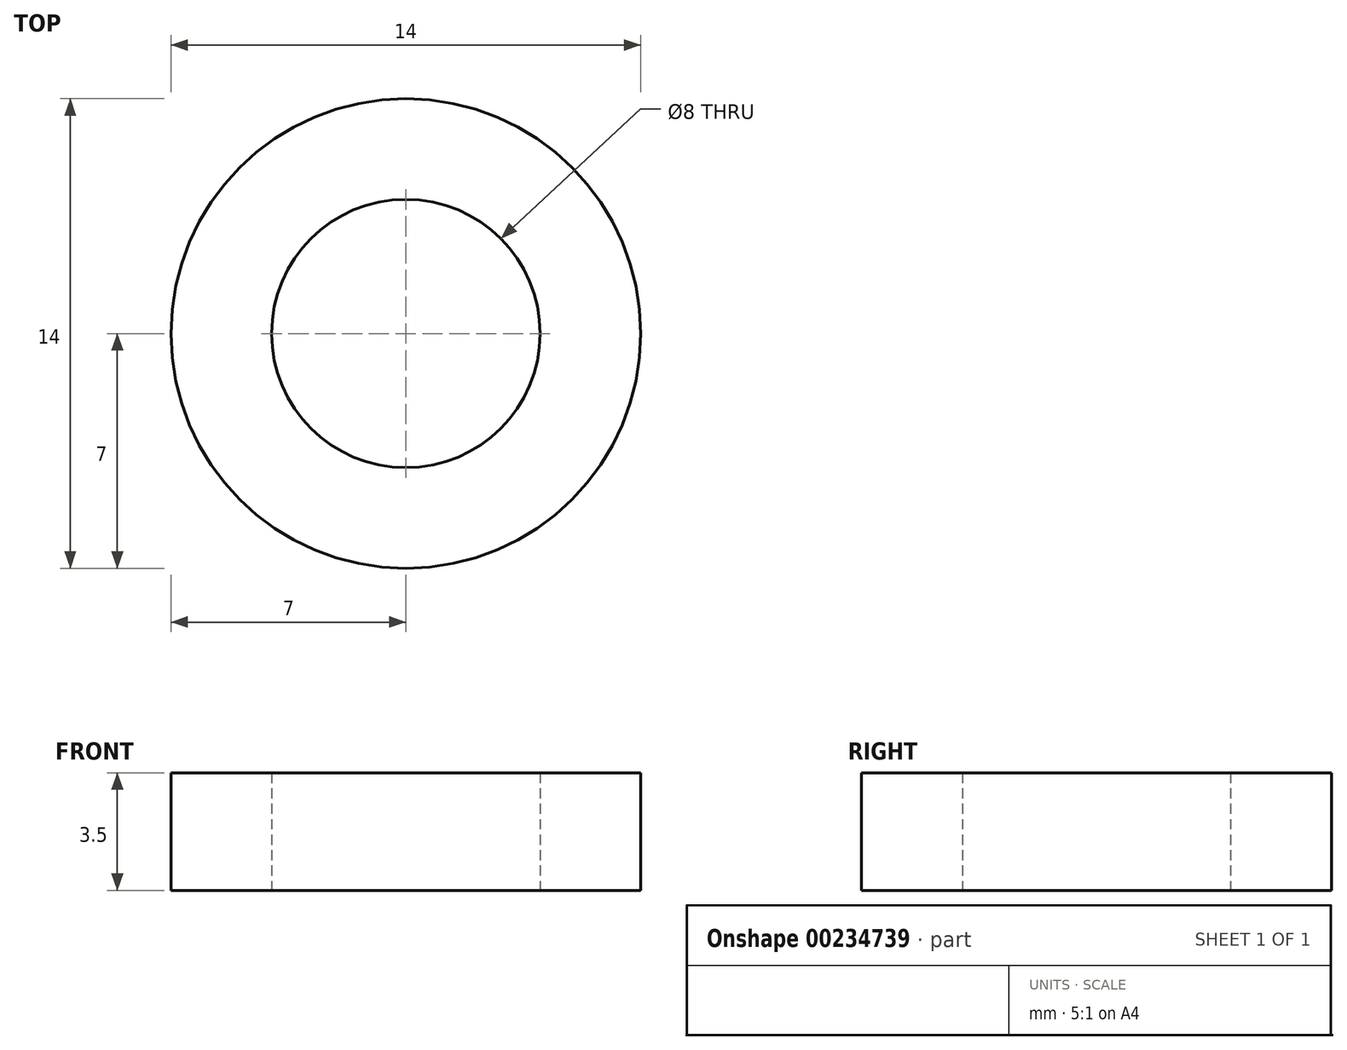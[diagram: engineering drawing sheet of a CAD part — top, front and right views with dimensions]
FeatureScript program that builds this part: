
annotation { "Feature Type Name" : "Feature", "Feature Type Description" : "" }
export const myFeature = defineFeature(function(context is Context, id is Id, definition is map)
    precondition{}
    {
        {
            var Q0;
            Q0=qCreatedBy(makeId("Top.planeOp"),FACE);
            var sketch = newSketch(context, id + "F0", { "sketchPlane" : qUnion([Q0])});
            skCircle(sketch, "E0", {"center": v(0, 0) * mm, "radius": 7 * mm});
            skCircle(sketch, "E1", {"center": v(0, 0) * mm, "radius": 4 * mm});
            skSolve(sketch);
        }
        {
            var Q0;
            Q0=qSketchRegion(id+"F0",true);
            extrude(context, id + "F1", {"entities" : qUnion([Q0]), "endBound" : BoundingType.SYMMETRIC, "depth" : 3.5 * mm});
        }
    });
